# Revit family: Faucet-Angle_Valve-KOHLER-July-K-80154IN_1
name_source: partatom
category: Plumbing Fixtures
units: mm (PartAtom-declared; Revit-internal decimal feet)

## family parameters
Cut with Voids When Loaded = No
Host = Face
OmniClass Number = 23.31.11.00
OmniClass Title = Faucets
Part Type = Normal
Room Calculation Point = No
Round Connector Dimension = Use Diameter
Shared = No

## types (2) — shared parameters
ADA Compliant = No
Assembly Code = D2010
CW Connection = Yes
Cold Water Inlet = Cold Water Inlet
Cold Water Outlet = Cold Water Outlet
Date Modified = 04/12/2023
Default Elevation = 36"
Description = Angle Valve (1 Pc Per Box)
Drain Included = No
Faucet Hole Spacing = 0"
Flow Rate = 0 GPM
HW Connection = Yes
Handle Clearance = 1 3/4"
Height = 1 3/4"
Hot Water Inlet = Hot Water Inlet
Length = 3"
Manufacturer = Kohler Co.
Master Format 2014 = 22 41 39
Master Format 2014 Name = Residential Faucets, Supplies, and Trim
Material = Premium Metal Construction
Pressure = 0.00 psi
Product Name = July
Product Page URL = https://www.kohler.co.in
Spout Reach = 3"
URL = https://www.kohler.co.in
Vent Connection = No
Waste Connection = No
Waste Water Outlet = Waste Water Outlet
WaterSense Certified = No
Width = 1 3/4"

## per-type parameters (varying)
| type | Finish | Model | Type |
| CP-Polished Chrome | Kohler-Metal-CP-Polished_Chrome | K-80154IN-4-CP | 1 |
| BV-Brushed Bronze | Kohler-Metal-BV-Brushed_Bronze | K-80154IN-4-BV | 2 |

## geometry (parser evidence)
native form markers: Sweep x6
no freeform markers — native parametric forms only
